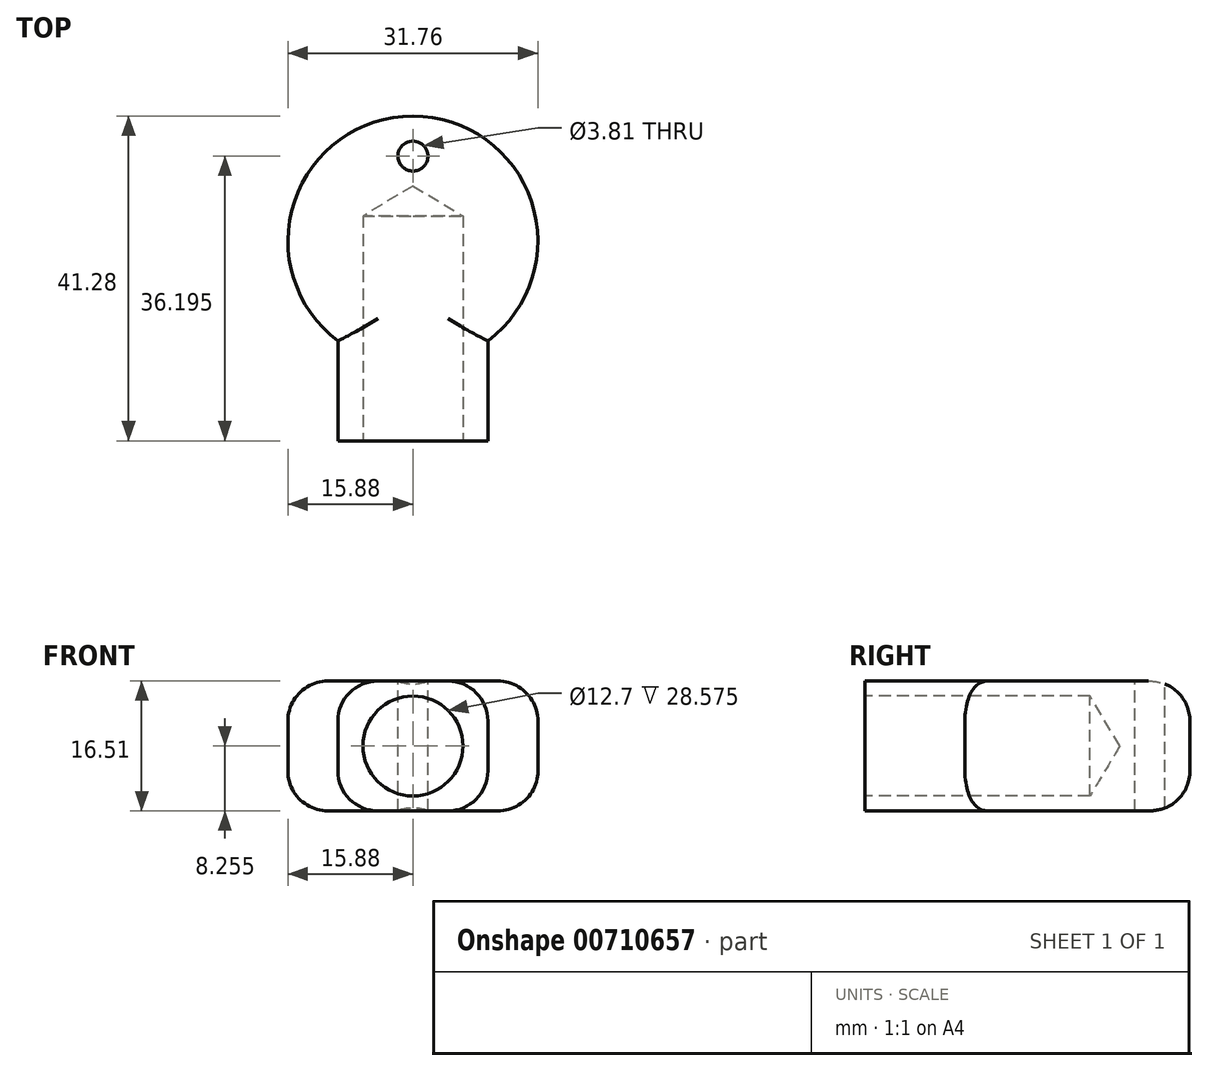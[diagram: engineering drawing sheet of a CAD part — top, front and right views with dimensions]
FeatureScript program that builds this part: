
annotation { "Feature Type Name" : "Feature", "Feature Type Description" : "" }
export const myFeature = defineFeature(function(context is Context, id is Id, definition is map)
    precondition{}
    {
        {
            var Q0;
            Q0=qCreatedBy(makeId("Top.planeOp"),FACE);
            var sketch = newSketch(context, id + "F0", { "sketchPlane" : qUnion([Q0])});
            skArc(sketch, "E0", {"start": v(9.53, -12.7) * mm, "mid": v(0, 15.88) * mm, "end": v(-9.53, -12.7) * mm});
            skLineSegment(sketch, "E1.top", {"start": v(9.52, -25.4) * mm, "end": v(-9.53, -25.4) * mm});
            skLineSegment(sketch, "E1.left", {"start": v(9.52, -12.7) * mm, "end": v(9.52, -25.4) * mm});
            skLineSegment(sketch, "E1.right", {"start": v(-9.53, -12.7) * mm, "end": v(-9.53, -25.4) * mm});
            skPoint(sketch, "E1.middle", {"position": v(0, -15.88) * mm});
            skPoint(sketch, "E2.orphan", {"position": v(9.52, -6.35) * mm});
            skPoint(sketch, "E3.orphan", {"position": v(-9.53, -6.35) * mm});
            skSolve(sketch);
        }
        {
            var Q0;
            Q0=makeQuery(id+"F0.imprint","IMPRINT",FACE,{"disambiguationData":[TD([[makeQuery(id+"F0.imprint","IMPRINT",EDGE,{"derivedFrom":sQuery(id+"F0.wireOp",EDGE,"E0")}),1.0]])]});
            extrude(context, id + "F1", {"entities" : qUnion([Q0]), "depth" : 16.5 * mm, "offsetDistance" : 25.4 * mm});
        }
        {
            var Q0;
            Q0=makeQuery(id+"F1.opExtrude","CAP_EDGE",EDGE,{"disambiguationData":[OSD([sQuery(id+"F0.wireOp",EDGE,"E0")])],"isStart":false});
            var Q1;
            Q1=makeQuery(id+"F1.opExtrude","CAP_EDGE",EDGE,{"disambiguationData":[OSD([sQuery(id+"F0.wireOp",EDGE,"E1.right")])],"isStart":false});
            var Q2;
            Q2=makeQuery(id+"F1.opExtrude","CAP_EDGE",EDGE,{"disambiguationData":[OSD([sQuery(id+"F0.wireOp",EDGE,"E1.left")])],"isStart":false});
            var Q3;
            Q3=makeQuery(id+"F1.opExtrude","CAP_EDGE",EDGE,{"disambiguationData":[OSD([sQuery(id+"F0.wireOp",EDGE,"E0")])],"isStart":true});
            var Q4;
            Q4=makeQuery(id+"F1.opExtrude","CAP_EDGE",EDGE,{"disambiguationData":[OSD([sQuery(id+"F0.wireOp",EDGE,"E1.right")])],"isStart":true});
            var Q5;
            Q5=makeQuery(id+"F1.opExtrude","CAP_EDGE",EDGE,{"disambiguationData":[OSD([sQuery(id+"F0.wireOp",EDGE,"E1.left")])],"isStart":true});
            fillet(context, id + "F2", {"entities" : qUnion([Q0, Q1, Q2, Q3, Q4, Q5]), "radius" : 5.08 * mm, "tangentPropagation" : true, "allowEdgeOverflow" : false});
        }
        {
            var Q0;
            Q0=makeQuery(id+"F1.opExtrude","CAP_FACE",FACE,{"disambiguationData":[OSD([sQuery(id+"F0.wireOp",EDGE,"E0"),sQuery(id+"F0.wireOp",EDGE,"E1.top"),sQuery(id+"F0.wireOp",EDGE,"E1.left"),sQuery(id+"F0.wireOp",EDGE,"E1.right")])],"isStart":false});
            var sketch = newSketch(context, id + "F3", { "sketchPlane" : qUnion([Q0])});
            skCircle(sketch, "E4", {"center": v(0, 10.8) * mm, "radius": 1.9 * mm});
            skSolve(sketch);
        }
        {
            var Q0;
            Q0=sQuery(id+"F3.wireOp",VERTEX,"E4.center");
            var Q1;
            Q1=makeQuery(id+"F1.opExtrude","SWEPT_BODY",BODY,{"disambiguationData":[OSD([sQuery(id+"F0.wireOp",EDGE,"E0"),sQuery(id+"F0.wireOp",EDGE,"E1.top"),sQuery(id+"F0.wireOp",EDGE,"E1.left"),sQuery(id+"F0.wireOp",EDGE,"E1.right")])]});
            hole(context, id + "F4", {"style" : HoleStyle.SIMPLE, "endStyle" : HoleEndStyle.THROUGH, "holeDiameter" : 3.8 * mm, "majorDiameter" : 6.35 * mm, "isTappedThrough" : true, "tappedDepth" : 12.7 * mm, "tapClearance" : 3, "locations" : qUnion([Q0]), "scope" : qUnion([Q1])});
        }
        {
            var Q0;
            Q0=makeQuery(id+"F1.opExtrude","SWEPT_FACE",FACE,{"disambiguationData":[OSD([sQuery(id+"F0.wireOp",EDGE,"E1.top")])]});
            var sketch = newSketch(context, id + "F5", { "sketchPlane" : qUnion([Q0])});
            skCircle(sketch, "E5", {"center": v(0, 8.26) * mm, "radius": 6.35 * mm});
            skPoint(sketch, "E6.orphan", {"position": v(-9.53, 11.43) * mm});
            skPoint(sketch, "E7.end.orphan", {"position": v(9.52, 5.08) * mm});
            skSolve(sketch);
        }
        {
            var Q0;
            Q0=sQuery(id+"F5.wireOp",VERTEX,"E5.center");
            var Q1;
            Q1=makeQuery(id+"F1.opExtrude","SWEPT_BODY",BODY,{"disambiguationData":[OSD([sQuery(id+"F0.wireOp",EDGE,"E0"),sQuery(id+"F0.wireOp",EDGE,"E1.top"),sQuery(id+"F0.wireOp",EDGE,"E1.left"),sQuery(id+"F0.wireOp",EDGE,"E1.right")])]});
            hole(context, id + "F6", {"style" : HoleStyle.SIMPLE, "endStyle" : HoleEndStyle.BLIND, "holeDiameter" : 12.7 * mm, "majorDiameter" : 6.35 * mm, "holeDepth" : 28.57 * mm, "isTappedThrough" : true, "tappedDepth" : 12.7 * mm, "tapClearance" : 3, "locations" : qUnion([Q0]), "scope" : qUnion([Q1])});
        }
    });
